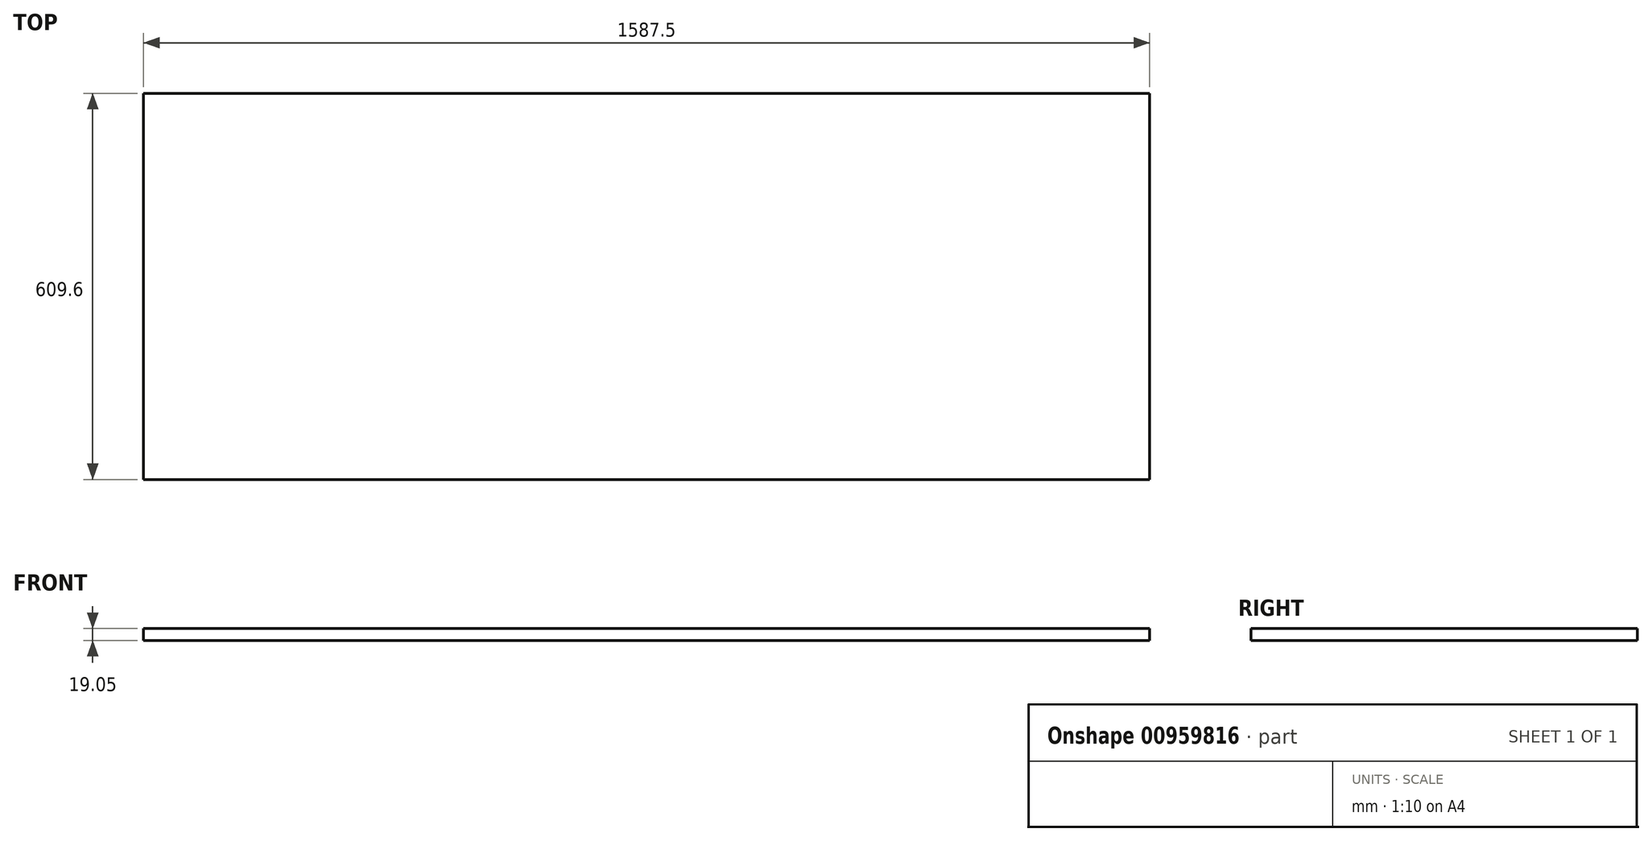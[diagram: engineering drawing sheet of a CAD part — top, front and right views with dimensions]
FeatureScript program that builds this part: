
annotation { "Feature Type Name" : "Feature", "Feature Type Description" : "" }
export const myFeature = defineFeature(function(context is Context, id is Id, definition is map)
    precondition{}
    {
        {
            var Q0;
            Q0=qCreatedBy(makeId("Top.planeOp"),FACE);
            var sketch = newSketch(context, id + "F0", { "sketchPlane" : qUnion([Q0])});
            skLineSegment(sketch, "E0.bottom", {"start": v(-793.75, 304.8) * mm, "end": v(793.75, 304.8) * mm});
            skLineSegment(sketch, "E0.top", {"start": v(-793.75, -304.8) * mm, "end": v(793.75, -304.8) * mm});
            skLineSegment(sketch, "E0.left", {"start": v(-793.75, 304.8) * mm, "end": v(-793.75, -304.8) * mm});
            skLineSegment(sketch, "E0.right", {"start": v(793.75, 304.8) * mm, "end": v(793.75, -304.8) * mm});
            skPoint(sketch, "E0.middle", {"position": v(0, 0) * mm});
            skSolve(sketch);
        }
        {
            var Q0;
            Q0=makeQuery(id+"F0.imprint","IMPRINT",FACE,{"disambiguationData":[TD([[makeQuery(id+"F0.imprint","IMPRINT",EDGE,{"derivedFrom":sQuery(id+"F0.wireOp",EDGE,"E0.bottom")}),-1.0]])]});
            extrude(context, id + "F1", {"entities" : qUnion([Q0]), "depth" : 19.05 * mm, "offsetDistance" : 25.4 * mm});
        }
    });
